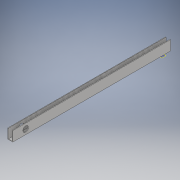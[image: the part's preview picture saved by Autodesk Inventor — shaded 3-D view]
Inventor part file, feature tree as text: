
AUTODESK INVENTOR PART (.ipt)
format: ipt  version: 2018 (Build 220112000, 112)  size: 130,048 bytes
history: native  units: in
note: dims shown in document units (in); Inventor stores cm internally (conversion verified against a paired STEP export)
features: sketch x4, extrude x4, plane x1
ambient origin geometry x8: Origin, YZ Plane, XZ Plane, XY Plane, X Axis, Y Axis, Z Axis, Center Point
bodies: Body1 (feature_tree)
feature tree (9):
  sketch  "Sketch1"  dims[d0=1.0in d1=32.0in]
  plane  "Work Plane3"
  extrude  "Extrusion3"  Depth=32.0in
  extrude  "Extrusion5"  Depth=0.125in TaperAngle=0.0deg
  extrude  "Extrusion6"  Depth=0.125in
  extrude  "Extrusion7"  Depth=1.0in TaperAngle=0.0deg
  sketch  "Sketch2"  dims[d2=0.125in d7=0.125in d8=0.0in]
  sketch  "Sketch4"  dims[d11=2.0in d12=0.0in d13=0.125in]
  sketch  "Sketch5"  dims[d14=0.125in d15=40.0in d16=0.0in d17=2.6in d18=1.0in d19=1.125in d20=40.0in d21=0.0in]
